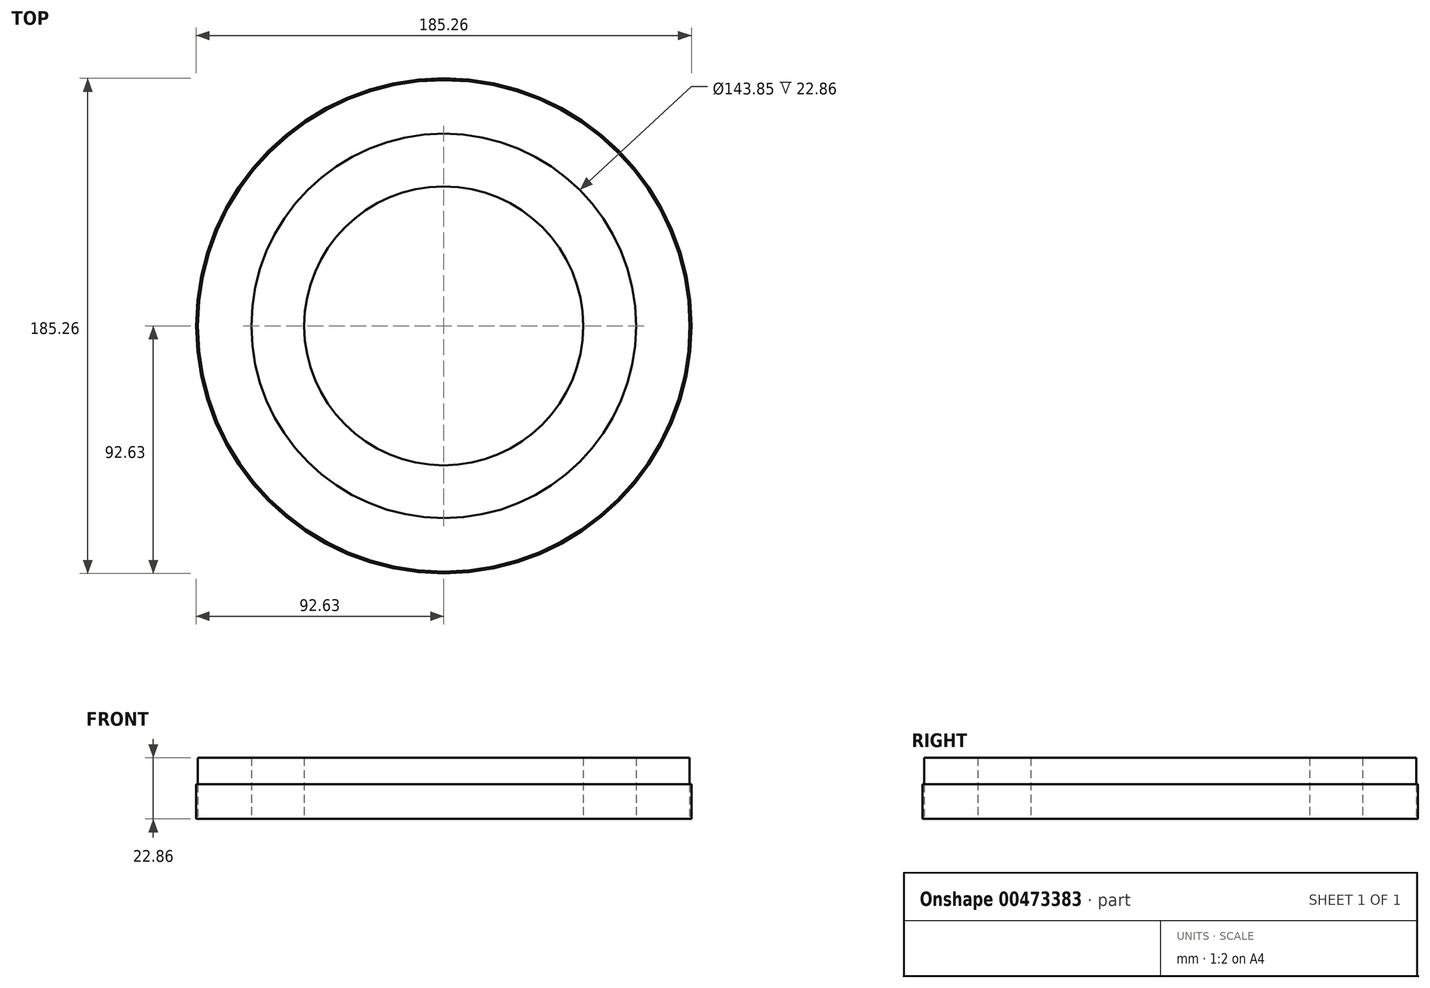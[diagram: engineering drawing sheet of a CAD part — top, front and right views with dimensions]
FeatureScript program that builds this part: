
annotation { "Feature Type Name" : "Feature", "Feature Type Description" : "" }
export const myFeature = defineFeature(function(context is Context, id is Id, definition is map)
    precondition{}
    {
        {
            var Q0;
            Q0=qCreatedBy(makeId("Top.planeOp"),FACE);
            var sketch = newSketch(context, id + "F0", { "sketchPlane" : qUnion([Q0])});
            skCircle(sketch, "E0", {"center": v(0, 0) * mm, "radius": 71.92 * mm});
            skCircle(sketch, "E1", {"center": v(0, 0) * mm, "radius": 52.17 * mm});
            skCircle(sketch, "E2", {"center": v(0, 0) * mm, "radius": 91.97 * mm});
            skSolve(sketch);
        }
        {
            var Q0;
            Q0=makeQuery(id+"F0.imprint","IMPRINT",FACE,{"disambiguationData":[TD([[makeQuery(id+"F0.imprint","IMPRINT",EDGE,{"derivedFrom":sQuery(id+"F0.wireOp",EDGE,"E0")}),-1.0]])]});
            var Q1;
            Q1=makeQuery(id+"F0.imprint","IMPRINT",FACE,{"disambiguationData":[TD([[makeQuery(id+"F0.imprint","IMPRINT",EDGE,{"derivedFrom":sQuery(id+"F0.wireOp",EDGE,"E1")}),1.0]])]});
            extrude(context, id + "F1", {"entities" : qUnion([Q0, Q1]), "depth" : 22.86 * mm});
        }
        {
            var Q0;
            Q0=qCreatedBy(makeId("Top.planeOp"),FACE);
            var sketch = newSketch(context, id + "F2", { "sketchPlane" : qUnion([Q0])});
            skCircle(sketch, "E3", {"center": v(0, 0) * mm, "radius": 92.63 * mm});
            skSolve(sketch);
        }
        {
            var Q0;
            Q0 = qSketchRegion(id + "F2", true);
            extrude(context, id + "F3", {"entities" : qUnion([Q0]), "depth" : 12.95 * mm});
        }
    });
